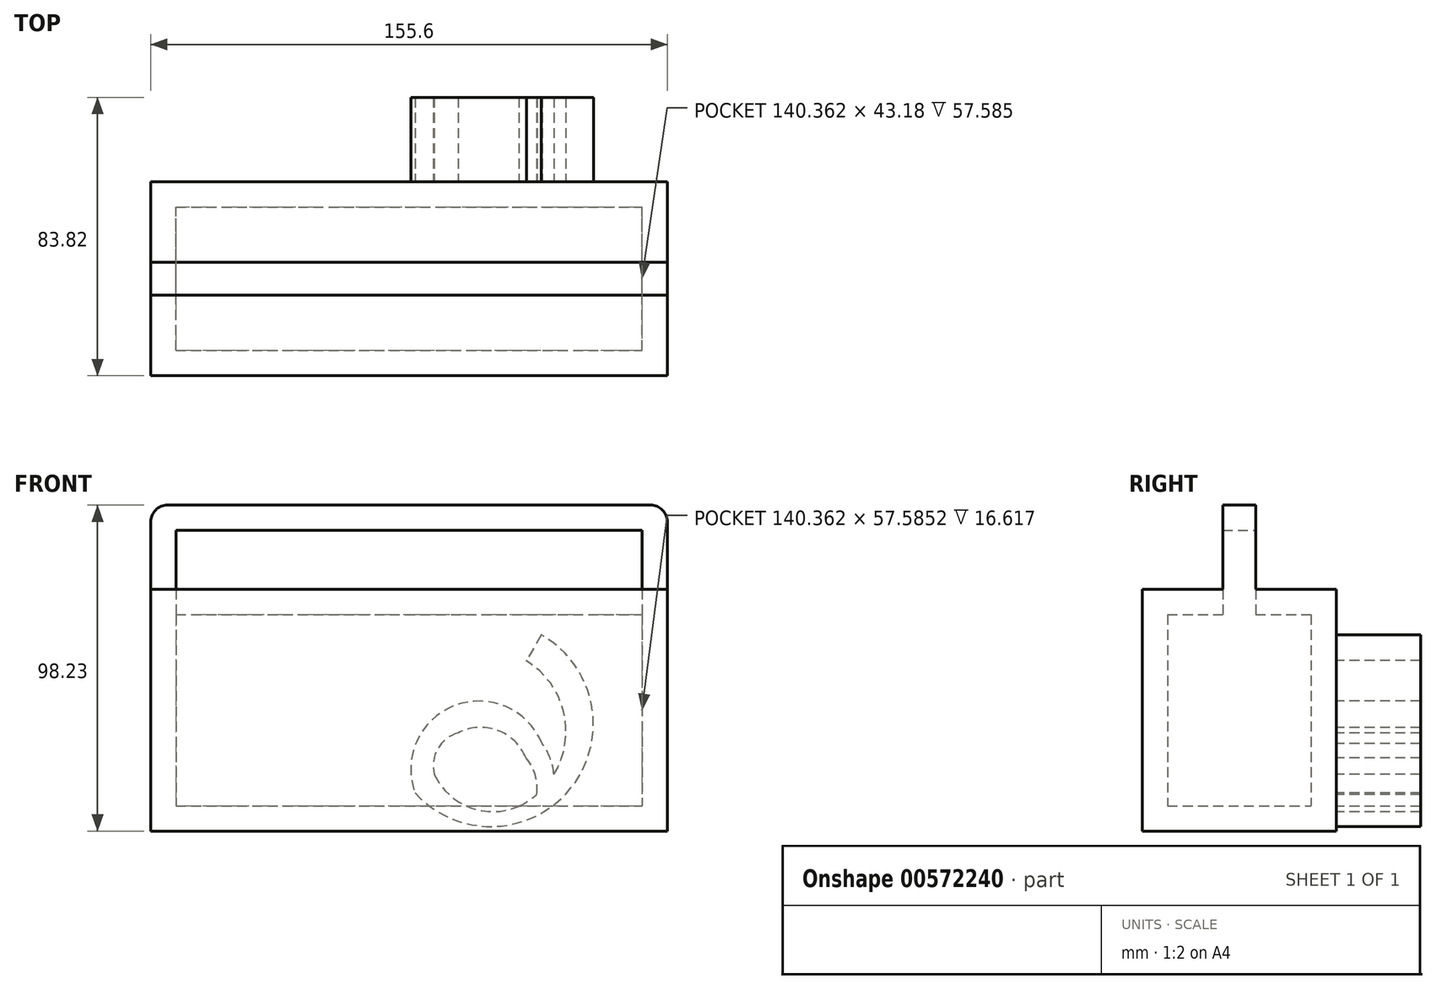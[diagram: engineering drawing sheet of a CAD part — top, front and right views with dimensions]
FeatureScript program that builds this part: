
annotation { "Feature Type Name" : "Feature", "Feature Type Description" : "" }
export const myFeature = defineFeature(function(context is Context, id is Id, definition is map)
    precondition{}
    {
        {
            var Q0;
            Q0=qCreatedBy(makeId("Front.planeOp"),FACE);
            var sketch = newSketch(context, id + "F0", { "sketchPlane" : qUnion([Q0])});
            skLineSegment(sketch, "E0.bottom", {"start": v(-79.61, 30.3) * mm, "end": v(76, 30.3) * mm});
            skLineSegment(sketch, "E0.top", {"start": v(-79.61, -42.52) * mm, "end": v(76, -42.52) * mm});
            skLineSegment(sketch, "E0.left", {"start": v(-79.61, 30.3) * mm, "end": v(-79.61, -42.52) * mm});
            skLineSegment(sketch, "E0.right", {"start": v(76, 30.3) * mm, "end": v(76, -42.52) * mm});
            skSolve(sketch);
        }
        {
            var Q0;
            Q0 = qSketchRegion(id + "F0", true);
            extrude(context, id + "F1", {"entities" : qUnion([Q0]), "depth" : 58.42 * mm, "offsetDistance" : 25.4 * mm});
        }
        {
            var Q0;
            Q0=makeQuery(id+"F1.opExtrude","SWEPT_FACE",FACE,{"disambiguationData":[OSD([sQuery(id+"F0.wireOp",EDGE,"E0.bottom")])]});
            var sketch = newSketch(context, id + "F2", { "sketchPlane" : qUnion([Q0])});
            skLineSegment(sketch, "E1", {"start": v(-79.61, -34.16) * mm, "end": v(76, -34.16) * mm});
            skLineSegment(sketch, "E2", {"start": v(-79.61, -24.24) * mm, "end": v(76, -24.24) * mm});
            skSolve(sketch);
        }
        {
            var Q0;
            Q0 = qSketchRegion(id + "F2", true);
            var Q1;
            {var subQ0=sQuery(id+"F2.wireOp",EDGE,"E1");Q1=makeQuery(id+"F2.imprint","IMPRINT",FACE,{"disambiguationData":[TD([[makeQuery(id+"F2.imprint","IMPRINT",EDGE,{"derivedFrom":subQ0}),1.0]])]});}
            extrude(context, id + "F3", {"entities" : qUnion([Q0, Q1]), "operationType" : NewBodyOperationType.ADD, "depth" : 25.4 * mm, "offsetDistance" : 25.4 * mm});
        }
        {
            var Q0;
            Q0=makeQuery(id+"F3.opExtrude","SWEPT_FACE",FACE,{"disambiguationData":[OSD([sQuery(id+"F2.wireOp",EDGE,"E1")])]});
            var Q1;
            Q1=makeQuery(id+"F3.opExtrude","SWEPT_FACE",FACE,{"disambiguationData":[OSD([sQuery(id+"F2.wireOp",EDGE,"E2")])]});
            shell(context, id + "F4", {"entities" : qUnion([Q0, Q1]), "thickness" : 7.62 * mm});
        }
        {
            var Q0;
            Q0=makeQuery(id+"F3.opExtrude","CAP_EDGE",EDGE,{"disambiguationData":[OSD([sQuery(id+"F0.wireOp",EDGE,"E0.bottom"),sQuery(id+"F0.wireOp",EDGE,"E0.right")])],"isStart":false});
            fillet(context, id + "F5", {"entities" : qUnion([Q0]), "radius" : 5.08 * mm, "tangentPropagation" : true, "allowEdgeOverflow" : false});
        }
        {
            var Q0;
            Q0=makeQuery(id+"F3.opExtrude","CAP_EDGE",EDGE,{"disambiguationData":[OSD([sQuery(id+"F0.wireOp",EDGE,"E0.bottom"),sQuery(id+"F0.wireOp",EDGE,"E0.left")])],"isStart":false});
            fillet(context, id + "F6", {"entities" : qUnion([Q0]), "radius" : 5.08 * mm, "tangentPropagation" : true, "allowEdgeOverflow" : false});
        }
        {
            var Q0;
            Q0=makeQuery(id+"F1.opExtrude","CAP_FACE",FACE,{"disambiguationData":[OSD([sQuery(id+"F0.wireOp",EDGE,"E0.bottom"),sQuery(id+"F0.wireOp",EDGE,"E0.top"),sQuery(id+"F0.wireOp",EDGE,"E0.left"),sQuery(id+"F0.wireOp",EDGE,"E0.right")])],"isStart":true});
            var sketch = newSketch(context, id + "F7", { "sketchPlane" : qUnion([Q0])});
            skArc(sketch, "E3", {"start": v(-38.04, 16.58) * mm, "mid": v(-46.95, -29.54) * mm, "end": v(0, -31.04) * mm});
            skArc(sketch, "E4", {"start": v(0, -31.04) * mm, "mid": v(-11.78, -4.78) * mm, "end": v(-38.25, -16.1) * mm});
            skArc(sketch, "E5", {"start": v(-12.95, -12.92) * mm, "mid": v(-24.81, -12.18) * mm, "end": v(-33.4, -20.41) * mm});
            skArc(sketch, "E6", {"start": v(-5.8, -25.46) * mm, "mid": v(-6.84, -17.74) * mm, "end": v(-12.95, -12.92) * mm});
            skArc(sketch, "E7", {"start": v(-31.23, -35.07) * mm, "mid": v(-16.57, -35.41) * mm, "end": v(-5.8, -25.46) * mm});
            skArc(sketch, "E8", {"start": v(-33.5, 8.8) * mm, "mid": v(-45.4, -13.8) * mm, "end": v(-31.23, -35.07) * mm});
            skArc(sketch, "E9", {"start": v(-38.25, -16.1) * mm, "mid": v(-40.68, -20.53) * mm, "end": v(-41.83, -25.46) * mm});
            skArc(sketch, "E10", {"start": v(-33.4, -20.41) * mm, "mid": v(-36.18, -25.63) * mm, "end": v(-36.67, -31.53) * mm});
            skLineSegment(sketch, "E11", {"start": v(-38.04, 16.58) * mm, "end": v(-33.5, 8.8) * mm});
            skSolve(sketch);
        }
        {
            var Q0;
            Q0=makeQuery(id+"F7.imprint","IMPRINT",FACE,{"disambiguationData":[TD([[makeQuery(id+"F7.imprint","IMPRINT",EDGE,{"derivedFrom":sQuery(id+"F7.wireOp",EDGE,"E3")}),1.0]])]});
            extrude(context, id + "F8", {"entities" : qUnion([Q0]), "operationType" : NewBodyOperationType.ADD, "depth" : 25.4 * mm, "offsetDistance" : 25.4 * mm});
        }
    });
